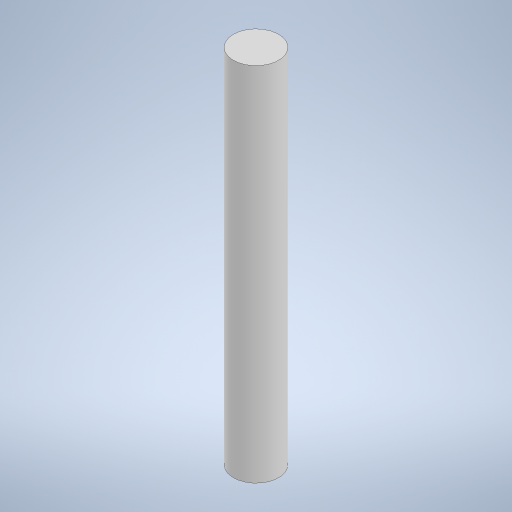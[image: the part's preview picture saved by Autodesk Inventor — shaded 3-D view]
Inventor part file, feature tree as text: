
AUTODESK INVENTOR PART (.ipt)
format: ipt  version: 2023 (Build 270158000, 158)  size: 221,184 bytes
history: native  units: mm
features: extrude x1, sketch x1
ambient origin geometry x8: Origin, YZ Plane, XZ Plane, XY Plane, X Axis, Y Axis, Z Axis, Center Point
bodies: Solid1 (feature_tree)
feature tree (2):
  extrude  "Extrusion1"  Depth=80.0mm TaperAngle=0.0deg
  sketch  "Sketch1"  dims[d0=10.0mm d1=80.0mm d2=0.0mm]
